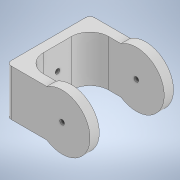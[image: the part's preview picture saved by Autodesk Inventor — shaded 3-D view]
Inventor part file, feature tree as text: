
AUTODESK INVENTOR PART (.ipt)
format: ipt  version: 2022 (Build 260153000, 153)  size: 153,600 bytes
history: native  units: mm
features: sketch x5, extrude x4, fillet x2
ambient origin geometry x8: Origin, YZ Plane, XZ Plane, XY Plane, X Axis, Y Axis, Z Axis, Center Point
bodies: Solid1 (feature_tree)
feature tree (11):
  extrude  "Extrusion1"  Depth=10.0mm
  fillet  "Fillet1"  Radius=10.0mm
  fillet  "Fillet2"  Radius=10.0mm
  extrude  "Extrusion2"  Depth=10.0mm TaperAngle=0.0deg
  extrude  "Extrusion3"  Depth=5.0mm
  extrude  "Extrusion4"  Depth=5.0mm TaperAngle=0.0deg
  sketch  "Sketch5"  dims[d15=5.0mm d16=161.25mm d17=0.0mm d18=5.0mm d19=161.25mm d20=0.0mm]
  sketch  "Sketch1"  dims[d0=45.0mm d1=45.0mm d2=10.0mm d3=10.0mm]
  sketch  "Sketch2"  dims[d4=10.0mm d5=60.0mm d6=0.0mm]
  sketch  "Sketch3"  dims[d7=20.0mm d8=5.0mm]
  sketch  "Sketch4"  dims[d10=5.0mm d12=161.25mm d13=0.0mm]
